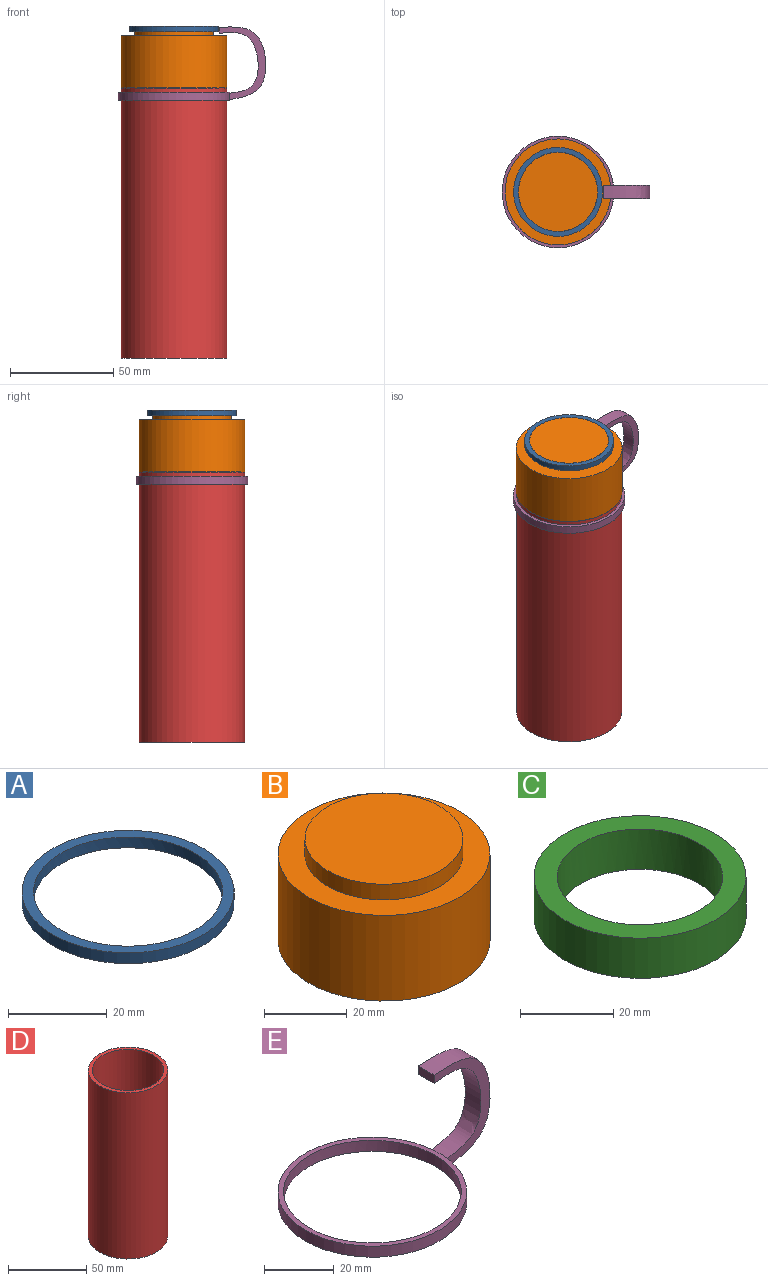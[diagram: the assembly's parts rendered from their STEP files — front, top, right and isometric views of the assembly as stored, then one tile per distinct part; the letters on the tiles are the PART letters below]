
ASSEMBLY  parts=5 mates=4
PART A: 4 faces, bbox 43x43x2.7 mm
  f0: plane 43.04x43.04mm, normal (0,0,-1), area 299.7mm2, adj f1,f3
  f1: cylinder r=21.52mm len=43.04mm, axis (0,0,1), area 362mm2, adj f0,f2
  f2: plane 43.04x43.04mm, normal (0,0,1), area 299.7mm2, adj f1,f3
  f3: cylinder r=19.18mm len=38.35mm, axis (0,0,-1), area 322.6mm2, adj f0,f2
PART B: 7 faces, bbox 51.3x51.3x30 mm
  f0: plane 51.29x51.29mm, normal (0,0,-1), area 424.5mm2, adj f1,f4
  f1: cylinder r=25.65mm len=51.29mm, axis (0,0,-1), area 4086mm2, adj f0,f2
  f2: plane 51.29x51.29mm, normal (0,0,1), area 918.4mm2, adj f1,f5
  f3: cone r=0mm half-angle=59deg, axis (0,0,-1), area 1915.3mm2, adj f4
  f4: cylinder r=22.86mm len=45.72mm, axis (0,0,-1), area 1459.3mm2, adj f0,f3
  f5: cylinder r=19.11mm len=38.23mm, axis (0,0,-1), area 553.7mm2, adj f2,f6
  f6: plane 38.23x38.23mm, normal (0,0,1), area 1147.8mm2, adj f5
PART C: 4 faces, bbox 45.5x45.5x10.6 mm
  f0: plane 45.53x45.53mm, normal (0,0,-1), area 634.8mm2, adj f1,f3
  f1: cylinder r=22.76mm len=45.53mm, axis (0,0,-1), area 1511.2mm2, adj f0,f2
  f2: plane 45.53x45.53mm, normal (0,0,1), area 634.8mm2, adj f1,f3
  f3: cylinder r=17.78mm len=35.56mm, axis (0,0,-1), area 1180.3mm2, adj f0,f2
PART D: 5 faces, bbox 50.9x50.9x130.4 mm
  f0: plane 50.91x50.91mm, normal (0,0,1), area 393.6mm2, adj f2,f4
  f1: plane 50.91x50.91mm, normal (0,0,-1), area 2035.4mm2, adj f2
  f2: cylinder r=25.45mm len=130.44mm, axis (0,0,-1), area 20860.5mm2, adj f0,f1
  f3: cone r=0mm half-angle=59deg, axis (0,0,1), area 1915.3mm2, adj f4
  f4: cylinder r=22.86mm len=96.52mm, axis (0,0,1), area 13863.5mm2, adj f0,f3
PART E: 9 faces, bbox 72.1x54x36.3 mm
  f0: extruded ~35.17x22.6mm, area 393.5mm2, adj f2,f3,f4,f5
  f1: extruded ~29.37x18.92mm, area 326.7mm2, adj f2,f3,f4,f5
  f2: plane 35.9x23.3mm, normal (0,-1,0), area 187mm2, adj f0,f1,f4,f5
  f3: plane 35.9x23.3mm, normal (0,1,0), area 187mm2, adj f0,f1,f4,f5
  f4: plane 6.35x2.88mm, normal (-1,0,0), area 18.3mm2, adj f0,f1,f2,f3
  f5: cylinder r=26.99mm len=53.98mm, axis (0,0,-1), area 632mm2, adj f0,f1,f2,f3,f6,f7
  f6: plane 53.98x53.98mm, normal (0,0,1), area 261.7mm2, adj f5,f8
  f7: plane 53.98x53.98mm, normal (0,0,-1), area 261.7mm2, adj f5,f8
  f8: cylinder r=25.4mm len=50.8mm, axis (0,0,1), area 613.2mm2, adj f6,f7
PLACE A rot(axis=(1,0,0),0deg) t=(-13.28,-49.4,21.64)mm
PLACE B t=(-13.28,-49.4,15.36)mm
PLACE C t=(-13.28,-49.4,-42)mm
PLACE D t=(-13.28,-49.4,-44.41)mm
PLACE E t=(-13.28,-49.4,20.65)mm
MATE cylindrical B.f1 <-> C.f1  axis (0,0,-1) through (-13.28,-49.4,20.44)mm
MATE cylindrical E.f5 <-> D.f2  axis (0,0,1) through (-13.28,-49.4,13.16)mm
MATE fastened A.f1 <-> B.f1  axis (0,0,1) through (-13.28,-49.4,45.33)mm
MATE fastened C.f1 <-> D.f2  axis (0,0,-1) through (-13.28,-49.4,15.15)mm
